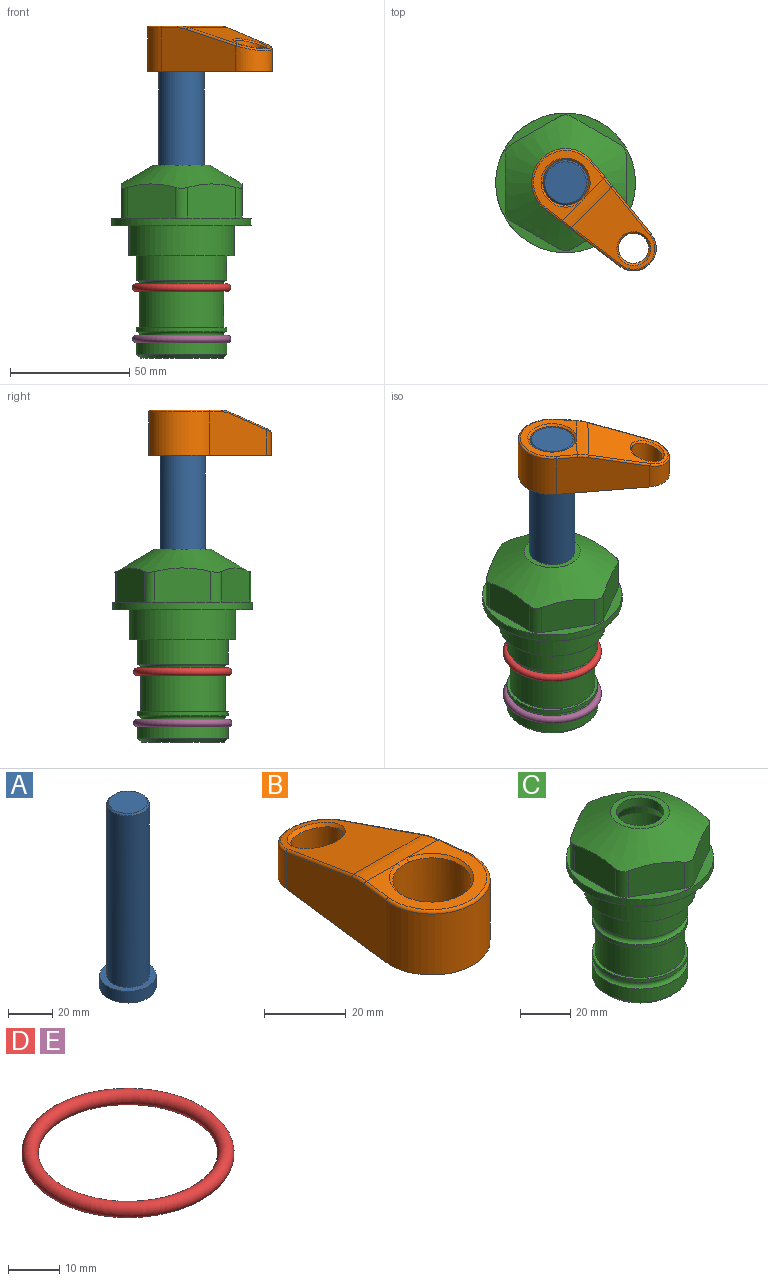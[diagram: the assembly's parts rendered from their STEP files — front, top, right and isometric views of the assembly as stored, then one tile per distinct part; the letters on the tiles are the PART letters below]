
ASSEMBLY  parts=5 mates=4
PART A: 6 faces, bbox 25.4x25.4x101.6 mm
  f0: plane 17.46x17.46mm, normal (0,0,1), area 239.5mm2, adj f5
  f1: plane 25.4x25.4mm, normal (0,0,-1), area 506.7mm2, adj f2
  f2: cylinder r=12.7mm len=25.4mm, axis (0,0,1), area 506.7mm2, adj f1,f3
  f3: plane 25.4x25.4mm, normal (0,0,1), area 221.7mm2, adj f2,f4
  f4: cylinder r=9.53mm len=94.46mm, axis (0,0,1), area 5653mm2, adj f3,f5
  f5: cone r=8.73mm half-angle=45deg, axis (0,0,-1), area 64.4mm2, adj f0,f4
PART B: 31 faces, bbox 31.7x65.5x19.8 mm
  f0: plane 39.12x18.26mm, normal (0.99,0.12,0), area 612.2mm2, adj f1,f4,f7,f11,f13,f15
  f1: cylinder r=9.53mm len=18.91mm, axis (0,0,-1), area 296.1mm2, adj f0,f2,f7,f17
  f2: plane 39.12x18.26mm, normal (-0.99,0.12,0), area 612.2mm2, adj f1,f4,f7,f12,f14,f16
  f3: cylinder r=6.35mm len=12.7mm, axis (0,0,-1), area 362.4mm2, adj f7,f18
  f4: cylinder r=14.29mm len=28.58mm, axis (0,0,-1), area 882.2mm2, adj f0,f2,f7,f10
  f5: cylinder r=9.53mm len=19.05mm, axis (0,0,-1), area 1092.6mm2, adj f7,f19,f20
  f6: plane 26.99x23.69mm, normal (0,0,1), area 216.2mm2, adj f9,f10,f11,f12,f19
  f7: plane 63.5x28.58mm, normal (0,0,-1), area 661.8mm2, adj f0,f1,f2,f3,f4,f5,f22,f23
  f8: plane 33.52x23.6mm, normal (0,0.26,0.97), area 486mm2, adj f9,f15,f16,f17,f18
  f9: cylinder r=19.05mm len=24.72mm, axis (1,0,0), area 120.4mm2, adj f6,f8,f13,f14,f20
  f10: torus R=13.49mm, axis (0,0,1), area 59mm2, adj f4,f6,f11,f12
  f11: cylinder r=0.79mm len=8.67mm, axis (0.12,-0.99,0), area 10.8mm2, adj f0,f6,f10,f13
  f12: cylinder r=0.79mm len=8.67mm, axis (0.12,0.99,0), area 10.8mm2, adj f2,f6,f10,f14
  f13: bspline ~4.95x1.42mm, area 6.1mm2, adj f0,f9,f11,f15
  f14: bspline ~4.95x1.42mm, area 6.1mm2, adj f2,f9,f12,f16
  f15: cylinder r=0.79mm len=25.95mm, axis (0.12,-0.96,0.26), area 32.9mm2, adj f0,f8,f13,f17
  f16: cylinder r=0.79mm len=25.95mm, axis (0.12,0.96,-0.26), area 32.9mm2, adj f2,f8,f14,f17
  f17: bspline ~18.91x8.38mm, area 30mm2, adj f1,f8,f15,f16
  f18: bspline ~14.29x14.29mm, area 48.3mm2, adj f3,f8
  f19: cone r=9.53mm half-angle=45deg, axis (0,0,1), area 66.5mm2, adj f5,f6,f20
  f20: bspline ~3.22x0.96mm, area 3.5mm2, adj f5,f9,f19
  f21: plane 2.75x2.72mm, normal (0,0,-1), area 2.9mm2, adj f23,f25,f28
  f22: plane 23.05x15.88mm, normal (-0.99,-0.12,0), area 323.6mm2, adj f7,f25,f26,f27,f28,f29
  f23: plane 23.05x15.88mm, normal (0.99,-0.12,0), area 323.6mm2, adj f7,f21,f25,f27,f28,f30
  f24: cylinder r=9.53mm len=10.69mm, axis (0,0,-1), area 114.7mm2, adj f7,f27,f29,f30
  f25: cylinder r=12.7mm len=20.59mm, axis (0,0,-1), area 381.1mm2, adj f7,f21,f22,f23,f26,f28
  f26: plane 2.75x2.72mm, normal (0,0,-1), area 2.9mm2, adj f22,f25,f28
  f27: plane 19.72x18.37mm, normal (0,-0.26,-0.97), area 291.8mm2, adj f22,f23,f24,f28,f29,f30
  f28: cylinder r=15.88mm len=19.92mm, axis (1,0,0), area 54.8mm2, adj f21,f22,f23,f25,f26,f27
  f29: cylinder r=1.59mm len=11mm, axis (0,0,-1), area 34.7mm2, adj f7,f22,f24,f27
  f30: cylinder r=1.59mm len=11mm, axis (0,0,-1), area 34.7mm2, adj f7,f23,f24,f27
PART C: 36 faces, bbox 58.7x58.7x81 mm
  f0: cylinder r=17.78mm len=35.56mm, axis (0,0,1), area 1670.8mm2, adj f23,f24,f31
  f1: cylinder r=19.05mm len=38.1mm, axis (0,0,1), area 1191.9mm2, adj f26,f27,f30
  f2: plane 58.66x58.66mm, normal (0,0,-1), area 1150.6mm2, adj f3,f28
  f3: cylinder r=29.33mm len=58.66mm, axis (0,0,-1), area 585.1mm2, adj f2,f4
  f4: plane 58.66x58.66mm, normal (0,0,1), area 475.9mm2, adj f3,f5,f6,f7,f8,f9,f10,f11
  f5: plane 20.32x14.34mm, normal (-0.5,0.87,0), area 324.4mm2, adj f4,f15,f16,f17
  f6: plane 20.32x14.34mm, normal (0.5,0.87,0), area 324.4mm2, adj f4,f14,f15,f17
  f7: plane 23.48x14.34mm, normal (1,0,0), area 324.4mm2, adj f4,f13,f14,f17
  f8: plane 20.32x14.34mm, normal (0.5,-0.87,0), area 324.4mm2, adj f4,f12,f13,f17
  f9: plane 20.32x14.34mm, normal (-0.5,-0.87,0), area 324.4mm2, adj f4,f11,f12,f17
  f10: plane 23.48x14.34mm, normal (-1,0,0), area 324.4mm2, adj f4,f11,f16,f17
  f11: cylinder r=5.08mm len=12.85mm, axis (0,0,-1), area 67.2mm2, adj f4,f9,f10,f17
  f12: cylinder r=5.08mm len=12.85mm, axis (0,0,-1), area 67.2mm2, adj f4,f8,f9,f17
  f13: cylinder r=5.08mm len=12.85mm, axis (0,0,-1), area 67.2mm2, adj f4,f7,f8,f17
  f14: cylinder r=5.08mm len=12.85mm, axis (0,0,-1), area 67.2mm2, adj f4,f6,f7,f17
  f15: cylinder r=5.08mm len=12.85mm, axis (0,0,-1), area 67.2mm2, adj f4,f5,f6,f17
  f16: cylinder r=5.08mm len=12.85mm, axis (0,0,-1), area 67.2mm2, adj f4,f5,f10,f17
  f17: cone r=11.73mm half-angle=60deg, axis (0,0,-1), area 2071.8mm2, adj f5,f6,f7,f8,f9,f10,f11,f12
  f18: plane 23.46x23.46mm, normal (0,0,1), area 147.4mm2, adj f17,f35
  f19: plane 34.93x34.93mm, normal (0,0,-1), area 958mm2, adj f29
  f20: cylinder r=19.05mm len=38.1mm, axis (0,0,1), area 760.1mm2, adj f21,f29
  f21: torus R=19.05mm, axis (0,0,1), area 565.3mm2, adj f20,f22
  f22: cylinder r=19.05mm len=38.1mm, axis (0,0,1), area 190mm2, adj f21,f23
  f23: plane 38.1x38.1mm, normal (0,0,1), area 146.9mm2, adj f0,f22
  f24: plane 38.1x38.1mm, normal (0,0,-1), area 146.9mm2, adj f0,f25
  f25: cylinder r=19.05mm len=38.1mm, axis (0,0,1), area 190mm2, adj f24,f26
  f26: torus R=19.05mm, axis (0,0,1), area 565.3mm2, adj f1,f25
  f27: plane 44.45x44.45mm, normal (0,0,-1), area 411.7mm2, adj f1,f28
  f28: cylinder r=22.23mm len=44.45mm, axis (0,0,1), area 1773.5mm2, adj f2,f27
  f29: cone r=19.05mm half-angle=45deg, axis (0,0,1), area 257.5mm2, adj f19,f20
  f30: cylinder r=3.17mm len=6.75mm, axis (-1,0,0), area 128mm2, adj f1,f33
  f31: cylinder r=3.17mm len=6.35mm, axis (-1,0,0), area 102.5mm2, adj f0,f33
  f32: plane 25.4x25.4mm, normal (0,0,1), area 506.7mm2, adj f33
  f33: cylinder r=12.7mm len=66.42mm, axis (0,0,-1), area 5236.2mm2, adj f30,f31,f32,f34
  f34: cone r=9.53mm half-angle=30deg, axis (0,0,-1), area 443.4mm2, adj f33,f35
  f35: cylinder r=9.53mm len=19.05mm, axis (0,0,-1), area 240.9mm2, adj f18,f34
PART D: 1 faces, bbox 44.7x44.7x3.2 mm
  f0: torus R=19.05mm, axis (0,0,1), area 1193.9mm2
PART E: same geometry as D
PLACE A rot(axis=(0,0,-1),134deg) t=(0,0,19.56)mm
PLACE B rot(axis=(0,0,-1),134deg) t=(0,0,20.35)mm
PLACE C at identity fixed
PLACE D t=(0,0,-1.59)mm
PLACE E t=(0,0,-23.18)mm
MATE fastened D.f0 <-> C.f0  axis (0,0,1) through (0,0,-26.1)mm
MATE cylindrical A.f2 <-> E.f0  axis (0,0,-1) through (0,0,-18.54)mm
MATE fastened B.f4 <-> A.f2  axis (0,0,1) through (0,0,83.06)mm
MATE fastened E.f0 <-> C.f0  axis (0,0,1) through (0,0,-47.69)mm
